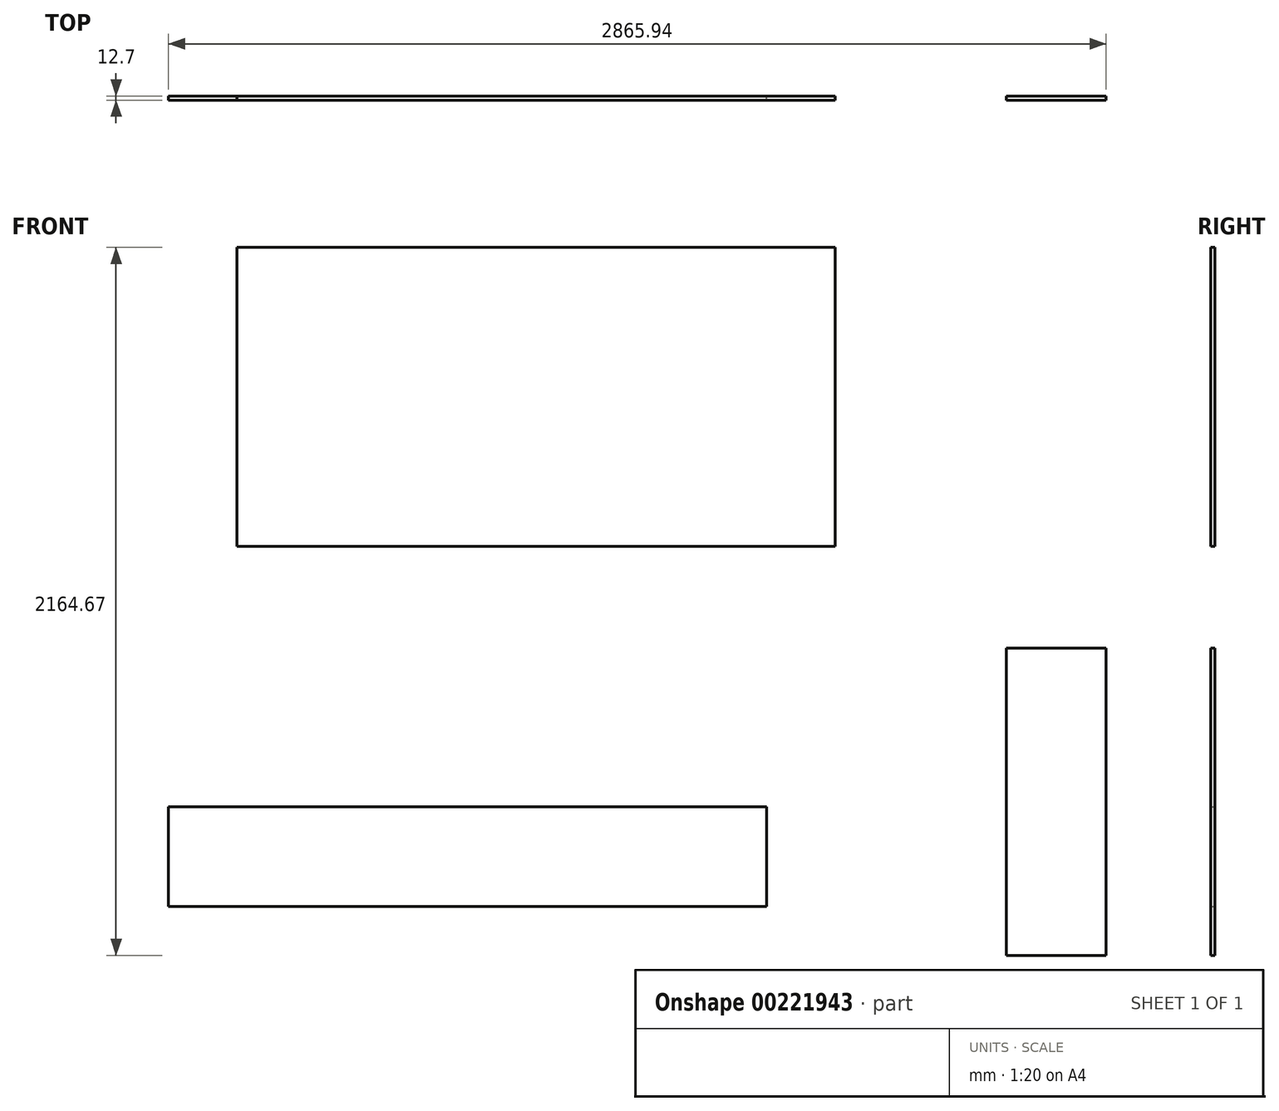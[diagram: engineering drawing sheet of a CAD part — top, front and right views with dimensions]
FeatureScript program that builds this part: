
annotation { "Feature Type Name" : "Feature", "Feature Type Description" : "" }
export const myFeature = defineFeature(function(context is Context, id is Id, definition is map)
    precondition{}
    {
        {
            var Q0;
            Q0=qCreatedBy(makeId("Front.planeOp"),FACE);
            var sketch = newSketch(context, id + "F0", { "sketchPlane" : qUnion([Q0])});
            skLineSegment(sketch, "E0.bottom", {"start": v(-1620.14, 1711.06) * mm, "end": v(208.66, 1711.06) * mm});
            skLineSegment(sketch, "E0.top", {"start": v(-1620.14, 796.66) * mm, "end": v(208.66, 796.66) * mm});
            skLineSegment(sketch, "E0.left", {"start": v(-1620.14, 1711.06) * mm, "end": v(-1620.14, 796.66) * mm});
            skLineSegment(sketch, "E0.right", {"start": v(208.66, 1711.06) * mm, "end": v(208.66, 796.66) * mm});
            skLineSegment(sketch, "E1.bottom", {"start": v(-1828.8, 0) * mm, "end": v(0, 0) * mm});
            skLineSegment(sketch, "E1.top", {"start": v(-1828.8, -304.8) * mm, "end": v(0, -304.8) * mm});
            skLineSegment(sketch, "E1.left", {"start": v(-1828.8, 0) * mm, "end": v(-1828.8, -304.8) * mm});
            skLineSegment(sketch, "E1.right", {"start": v(0, 0) * mm, "end": v(0, -304.8) * mm});
            skLineSegment(sketch, "E2.bottom", {"start": v(732.34, 486.19) * mm, "end": v(1037.14, 486.19) * mm});
            skLineSegment(sketch, "E2.top", {"start": v(732.34, -453.61) * mm, "end": v(1037.14, -453.61) * mm});
            skLineSegment(sketch, "E2.left", {"start": v(732.34, 486.19) * mm, "end": v(732.34, -453.61) * mm});
            skLineSegment(sketch, "E2.right", {"start": v(1037.14, 486.19) * mm, "end": v(1037.14, -453.61) * mm});
            skSolve(sketch);
        }
        {
            var Q0;
            Q0=makeQuery(id+"F0.imprint","IMPRINT",FACE,{"disambiguationData":[TD([[makeQuery(id+"F0.imprint","IMPRINT",EDGE,{"derivedFrom":sQuery(id+"F0.wireOp",EDGE,"E0.bottom")}),-1.0]])]});
            var Q1;
            Q1=makeQuery(id+"F0.imprint","IMPRINT",FACE,{"disambiguationData":[TD([[makeQuery(id+"F0.imprint","IMPRINT",EDGE,{"derivedFrom":sQuery(id+"F0.wireOp",EDGE,"E2.bottom")}),-1.0]])]});
            var Q2;
            Q2=makeQuery(id+"F0.imprint","IMPRINT",FACE,{"disambiguationData":[TD([[makeQuery(id+"F0.imprint","IMPRINT",EDGE,{"derivedFrom":sQuery(id+"F0.wireOp",EDGE,"E1.bottom")}),-1.0]])]});
            extrude(context, id + "F1", {"entities" : qUnion([Q0, Q1, Q2]), "depth" : 12.7 * mm});
        }
    });
